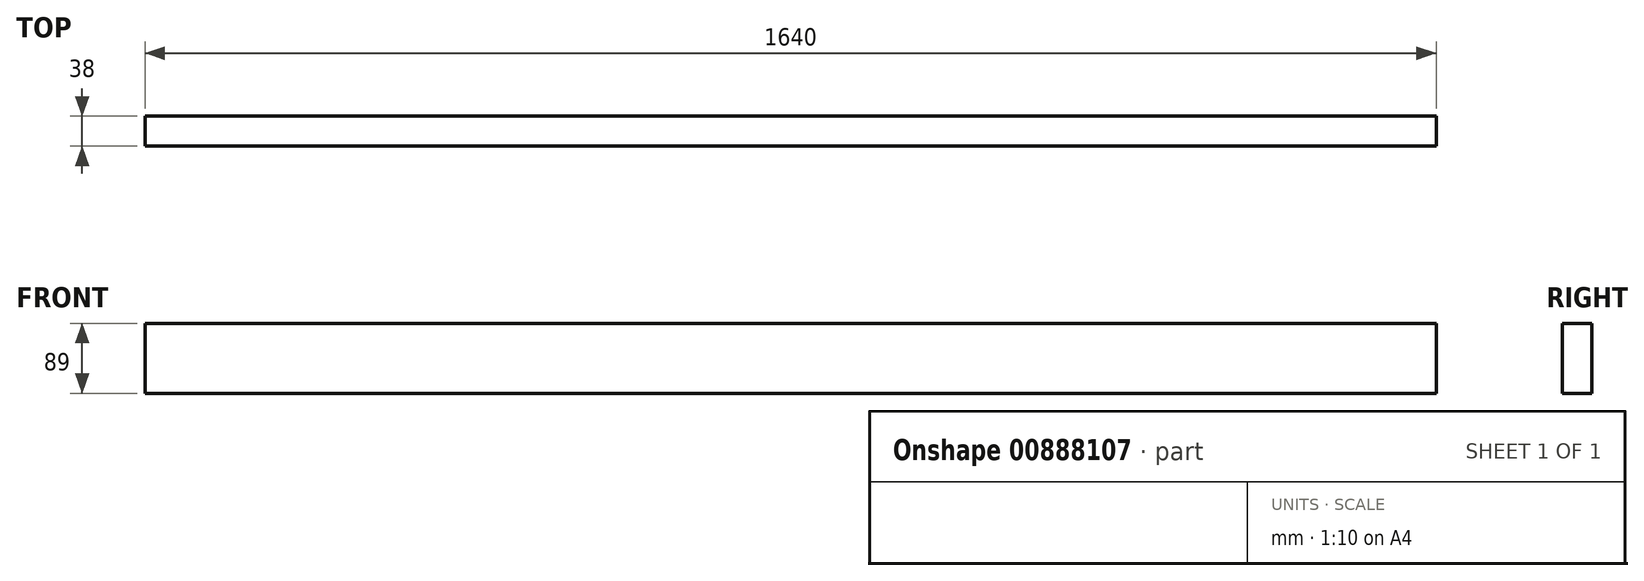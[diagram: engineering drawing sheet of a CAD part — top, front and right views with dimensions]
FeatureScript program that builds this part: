
annotation { "Feature Type Name" : "Feature", "Feature Type Description" : "" }
export const myFeature = defineFeature(function(context is Context, id is Id, definition is map)
    precondition{}
    {
        {
            var Q0;
            Q0=qCreatedBy(makeId("Front.planeOp"),FACE);
            var sketch = newSketch(context, id + "F0", { "sketchPlane" : qUnion([Q0])});
            skLineSegment(sketch, "E0.bottom", {"start": v(-196.13, 55.88) * mm, "end": v(1443.87, 55.88) * mm});
            skLineSegment(sketch, "E0.top", {"start": v(-196.13, -33.12) * mm, "end": v(1443.87, -33.12) * mm});
            skLineSegment(sketch, "E0.left", {"start": v(-196.13, 55.88) * mm, "end": v(-196.13, -33.12) * mm});
            skLineSegment(sketch, "E0.right", {"start": v(1443.87, 55.88) * mm, "end": v(1443.87, -33.12) * mm});
            skSolve(sketch);
        }
        {
            var Q0;
            Q0=makeQuery(id+"F0.imprint","IMPRINT",FACE,{"disambiguationData":[TD([[makeQuery(id+"F0.imprint","IMPRINT",EDGE,{"derivedFrom":sQuery(id+"F0.wireOp",EDGE,"E0.bottom")}),-1.0]])]});
            extrude(context, id + "F1", {"entities" : qUnion([Q0]), "depth" : 38 * mm, "offsetDistance" : 25 * mm});
        }
    });
